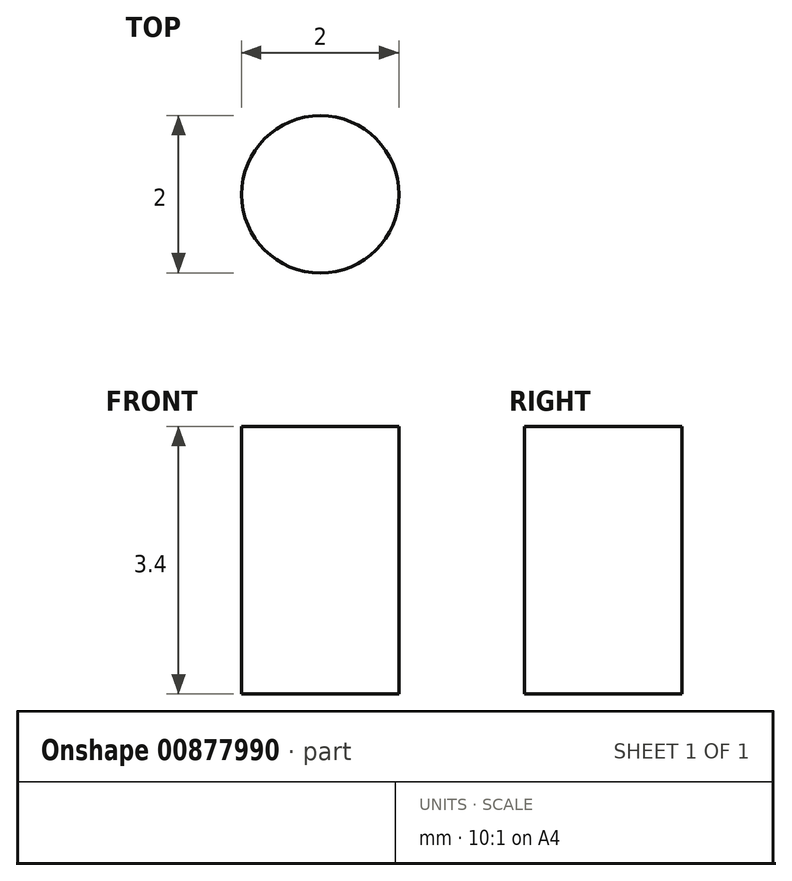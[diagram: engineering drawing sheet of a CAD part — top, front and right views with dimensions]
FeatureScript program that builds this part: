
annotation { "Feature Type Name" : "Feature", "Feature Type Description" : "" }
export const myFeature = defineFeature(function(context is Context, id is Id, definition is map)
    precondition{}
    {
        {
            var Q0;
            Q0=qCreatedBy(makeId("Top.planeOp"),FACE);
            var sketch = newSketch(context, id + "F0", { "sketchPlane" : qUnion([Q0])});
            skCircle(sketch, "E0", {"center": v(-48.6, 33.49) * mm, "radius": 1 * mm});
            skSolve(sketch);
        }
        {
            var Q0;
            Q0=makeQuery(id+"F0.imprint","IMPRINT",FACE,{"disambiguationData":[TD([[makeQuery(id+"F0.imprint","IMPRINT",EDGE,{"derivedFrom":sQuery(id+"F0.wireOp",EDGE,"E0")}),1.0]])]});
            extrude(context, id + "F1", {"entities" : qUnion([Q0]), "depth" : 3.4 * mm, "offsetDistance" : 25 * mm});
        }
    });
